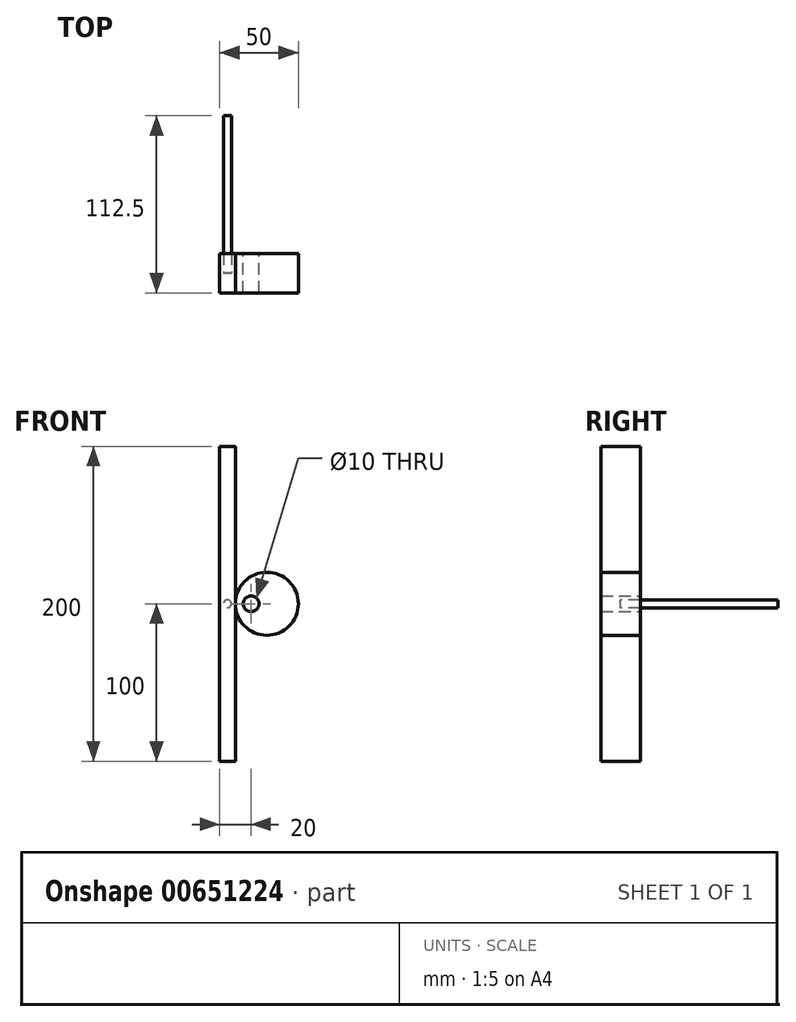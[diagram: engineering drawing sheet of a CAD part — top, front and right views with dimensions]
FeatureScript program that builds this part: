
annotation { "Feature Type Name" : "Feature", "Feature Type Description" : "" }
export const myFeature = defineFeature(function(context is Context, id is Id, definition is map)
    precondition{}
    {
        {
            var Q0;
            Q0=qCreatedBy(makeId("Front.planeOp"),FACE);
            var sketch = newSketch(context, id + "F0", { "sketchPlane" : qUnion([Q0])});
            skLineSegment(sketch, "E0.bottom", {"start": v(-5, 100) * mm, "end": v(5, 100) * mm});
            skLineSegment(sketch, "E0.top", {"start": v(-5, -100) * mm, "end": v(5, -100) * mm});
            skLineSegment(sketch, "E0.left", {"start": v(-5, 100) * mm, "end": v(-5, -100) * mm});
            skLineSegment(sketch, "E0.right", {"start": v(5, 100) * mm, "end": v(5, -100) * mm});
            skCircle(sketch, "E1", {"center": v(25, 0) * mm, "radius": 20 * mm});
            skCircle(sketch, "E2", {"center": v(15, 0) * mm, "radius": 5 * mm});
            skSolve(sketch);
        }
        {
            var Q0;
            {var subQ1=sQuery(id+"F0.wireOp",EDGE,"E0.bottom");Q0=makeQuery(id+"F0.imprint","IMPRINT",FACE,{"disambiguationData":[TD([[makeQuery(id+"F0.imprint","IMPRINT",EDGE,{"derivedFrom":subQ1}),-1.0]])]});}
            var Q1;
            Q1=makeQuery(id+"F0.imprint","IMPRINT",FACE,{"disambiguationData":[TD([[makeQuery(id+"F0.imprint","IMPRINT",EDGE,{"derivedFrom":sQuery(id+"F0.wireOp",EDGE,"E1")}),1.0]])]});
            extrude(context, id + "F1", {"entities" : qUnion([Q0, Q1]), "endBound" : BoundingType.SYMMETRIC, "depth" : 25 * mm, "offsetDistance" : 25 * mm});
        }
        {
            var Q0;
            Q0=qCreatedBy(makeId("Front.planeOp"),FACE);
            var sketch = newSketch(context, id + "F2", { "sketchPlane" : qUnion([Q0])});
            skCircle(sketch, "E3", {"center": v(0, 0) * mm, "radius": 2.5 * mm});
            skSolve(sketch);
        }
        {
            var Q0;
            Q0 = qSketchRegion(id + "F2", true);
            var Q1;
            Q1=sQuery(id+"F2.wireOp",EDGE,"E3");
            extrude(context, id + "F3", {"entities" : qUnion([Q0]), "surfaceEntities" : qUnion([Q1]), "depth" : -100 * mm, "hasOffset" : true, "offsetDistance" : 25 * mm});
        }
    });
